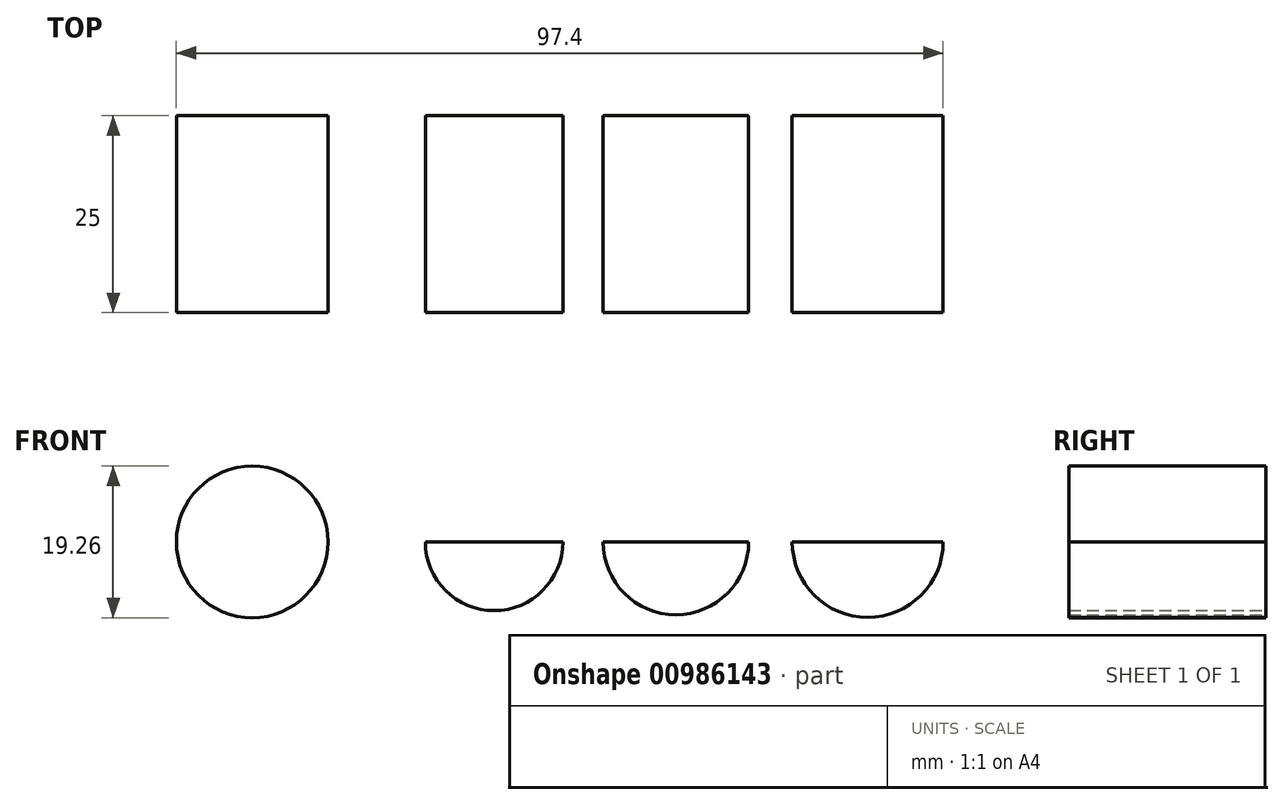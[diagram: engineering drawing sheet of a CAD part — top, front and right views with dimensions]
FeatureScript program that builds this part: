
annotation { "Feature Type Name" : "Feature", "Feature Type Description" : "" }
export const myFeature = defineFeature(function(context is Context, id is Id, definition is map)
    precondition{}
    {
        {
            var Q0;
            Q0=qCreatedBy(makeId("Front.planeOp"),FACE);
            var sketch = newSketch(context, id + "F0", { "sketchPlane" : qUnion([Q0])});
            skCircle(sketch, "E0", {"center": v(0, 0) * mm, "radius": 8.73 * mm});
            skLineSegment(sketch, "E1", {"start": v(0, 0) * mm, "end": v(23.09, 0) * mm});
            skLineSegment(sketch, "E2", {"start": v(23.09, 0) * mm, "end": v(47.45, 0) * mm});
            skCircle(sketch, "E3", {"center": v(23.09, 0) * mm, "radius": 9.25 * mm});
            skCircle(sketch, "E4", {"center": v(47.45, 0) * mm, "radius": 9.59 * mm});
            skLineSegment(sketch, "E5", {"start": v(0, 0) * mm, "end": v(-30.74, 0) * mm});
            skCircle(sketch, "E6", {"center": v(-30.74, 0) * mm, "radius": 9.63 * mm});
            skLineSegment(sketch, "E7", {"start": v(47.45, 0) * mm, "end": v(68.41, 0) * mm});
            skLineSegment(sketch, "E8", {"start": v(68.41, 0) * mm, "end": v(68.41, 25.07) * mm});
            skLineSegment(sketch, "E9", {"start": v(68.41, 25.07) * mm, "end": v(61.33, 25.07) * mm});
            skLineSegment(sketch, "E10", {"start": v(61.33, 25.07) * mm, "end": v(61.33, 39.8) * mm});
            skLineSegment(sketch, "E11", {"start": v(61.33, 39.8) * mm, "end": v(68.41, 43.77) * mm});
            skLineSegment(sketch, "E12", {"start": v(68.41, 43.77) * mm, "end": v(68.41, 50.28) * mm});
            skLineSegment(sketch, "E13", {"start": v(68.41, 50.28) * mm, "end": v(37.25, 55.38) * mm});
            skLineSegment(sketch, "E14", {"start": v(37.25, 55.38) * mm, "end": v(14.3, 50.28) * mm});
            skLineSegment(sketch, "E15", {"start": v(14.3, 50.28) * mm, "end": v(17.24, 43.77) * mm});
            skLineSegment(sketch, "E16", {"start": v(17.24, 43.77) * mm, "end": v(23.65, 43.77) * mm});
            skLineSegment(sketch, "E17", {"start": v(23.65, 43.77) * mm, "end": v(23.65, 25.35) * mm});
            skLineSegment(sketch, "E18", {"start": v(23.65, 25.35) * mm, "end": v(17.24, 25.35) * mm});
            skLineSegment(sketch, "E19", {"start": v(17.24, 25.35) * mm, "end": v(17.24, 38.1) * mm});
            skLineSegment(sketch, "E20", {"start": v(16, 36.4) * mm, "end": v(-12.32, 36.4) * mm});
            skLineSegment(sketch, "E21", {"start": v(-12.32, 36.4) * mm, "end": v(-12.32, 48.58) * mm});
            skLineSegment(sketch, "E22", {"start": v(-12.32, 48.58) * mm, "end": v(-8.36, 53.4) * mm});
            skLineSegment(sketch, "E23", {"start": v(-8.36, 53.4) * mm, "end": v(-4.1, 53.4) * mm});
            skLineSegment(sketch, "E24", {"start": v(-4.1, 53.4) * mm, "end": v(-4.1, 59.63) * mm});
            skLineSegment(sketch, "E25", {"start": v(-4.1, 59.63) * mm, "end": v(-26.2, 59.63) * mm});
            skLineSegment(sketch, "E26", {"start": v(-26.2, 59.63) * mm, "end": v(-26.2, 53.4) * mm});
            skLineSegment(sketch, "E27", {"start": v(-26.2, 53.4) * mm, "end": v(-21.67, 48.86) * mm});
            skLineSegment(sketch, "E28", {"start": v(-21.67, 48.86) * mm, "end": v(-21.67, 36.4) * mm});
            skLineSegment(sketch, "E29", {"start": v(-21.67, 36.4) * mm, "end": v(-44.33, 36.4) * mm});
            skLineSegment(sketch, "E30", {"start": v(-44.33, 36.4) * mm, "end": v(-48.86, 18.27) * mm});
            skLineSegment(sketch, "E31", {"start": v(-48.86, 18.27) * mm, "end": v(-48.86, 11.19) * mm});
            skLineSegment(sketch, "E32", {"start": v(-48.86, 11.19) * mm, "end": v(-62.75, 0) * mm});
            skLineSegment(sketch, "E33", {"start": v(-62.75, 0) * mm, "end": v(-30.74, 0) * mm});
            skLineSegment(sketch, "E34", {"start": v(16, 36.4) * mm, "end": v(17.24, 38.1) * mm});
            skSolve(sketch);
        }
        {
            var Q0;
            {var subQ0=sQuery(id+"F0.wireOp",EDGE,"E7");var subQ1=sQuery(id+"F0.wireOp",EDGE,"E2");var subQ2=makeQuery(id+"F0.imprint","INTERSECT",VERTEX,{"derivedFrom":[subQ1,subQ0]});Q0=makeQuery(id+"F0.imprint","IMPRINT",FACE,{"disambiguationData":[TD([[makeQuery(id+"F0.imprint","IMPRINT",EDGE,{"disambiguationData":[TD([[subQ2,1.0]])],"derivedFrom":subQ1}),-1.0]])]});}
            var Q1;
            {var subQ0=sQuery(id+"F0.wireOp",EDGE,"E1");var subQ1=sQuery(id+"F0.wireOp",EDGE,"E0");var subQ2=makeQuery(id+"F0.imprint","INTERSECT",VERTEX,{"derivedFrom":[subQ1,subQ0]});Q1=makeQuery(id+"F0.imprint","IMPRINT",FACE,{"disambiguationData":[TD([[makeQuery(id+"F0.imprint","IMPRINT",EDGE,{"disambiguationData":[TD([[subQ2,1.0]])],"derivedFrom":subQ1}),1.0]])]});}
            var Q2;
            {var subQ0=sQuery(id+"F0.wireOp",EDGE,"E33");var subQ1=sQuery(id+"F0.wireOp",EDGE,"E5");var subQ2=makeQuery(id+"F0.imprint","INTERSECT",VERTEX,{"derivedFrom":[subQ1,subQ0]});Q2=makeQuery(id+"F0.imprint","IMPRINT",FACE,{"disambiguationData":[TD([[makeQuery(id+"F0.imprint","IMPRINT",EDGE,{"disambiguationData":[TD([[subQ2,1.0]])],"derivedFrom":subQ1}),1.0]])]});}
            var Q3;
            {var subQ0=sQuery(id+"F0.wireOp",EDGE,"E33");var subQ1=sQuery(id+"F0.wireOp",EDGE,"E5");var subQ2=makeQuery(id+"F0.imprint","INTERSECT",VERTEX,{"derivedFrom":[subQ1,subQ0]});Q3=makeQuery(id+"F0.imprint","IMPRINT",FACE,{"disambiguationData":[TD([[makeQuery(id+"F0.imprint","IMPRINT",EDGE,{"disambiguationData":[TD([[subQ2,1.0]])],"derivedFrom":subQ1}),-1.0]])]});}
            var Q4;
            {var subQ0=sQuery(id+"F0.wireOp",EDGE,"E2");var subQ1=sQuery(id+"F0.wireOp",EDGE,"E1");var subQ2=makeQuery(id+"F0.imprint","INTERSECT",VERTEX,{"derivedFrom":[subQ1,subQ0]});Q4=makeQuery(id+"F0.imprint","IMPRINT",FACE,{"disambiguationData":[TD([[makeQuery(id+"F0.imprint","IMPRINT",EDGE,{"disambiguationData":[TD([[subQ2,1.0]])],"derivedFrom":subQ1}),-1.0]])]});}
            extrude(context, id + "F1", {"entities" : qUnion([Q0, Q1, Q2, Q3, Q4]), "depth" : 25 * mm, "offsetDistance" : 25 * mm});
        }
    });
